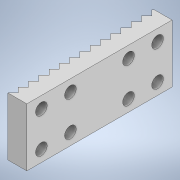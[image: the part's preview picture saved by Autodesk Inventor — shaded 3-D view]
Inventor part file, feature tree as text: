
AUTODESK INVENTOR PART (.ipt)
format: ipt  version: 2020 (Build 240168000, 168)  size: 179,200 bytes
history: native  units: in
note: dims shown in document units (in); Inventor stores cm internally (conversion verified against a paired STEP export)
features: extrude x2, sketch x2
ambient origin geometry x8: Origin, YZ Plane, XZ Plane, XY Plane, X Axis, Y Axis, Z Axis, Center Point
bodies: Solid1 (feature_tree)
feature tree (4):
  extrude  "Extrusion1"  Depth=1.9685in
  extrude  "Extrusion2"  Depth=0.0984in
  sketch  "Sketch1"  dims[d0=0.1575in d1=1.9685in]
  sketch  "Sketch2"  dims[d2=0.0984in d3=0.0984in d4=45.0deg d5=0.0984in d6=0.7874in d7=0.0in d8=0.1575in d9=0.1575in d10=0.1575in d11=0.1575in d12=0.1575in d13=0.1575in d14=0.1575in d15=0.1575in d16=0.7874in d17=0.0in]
